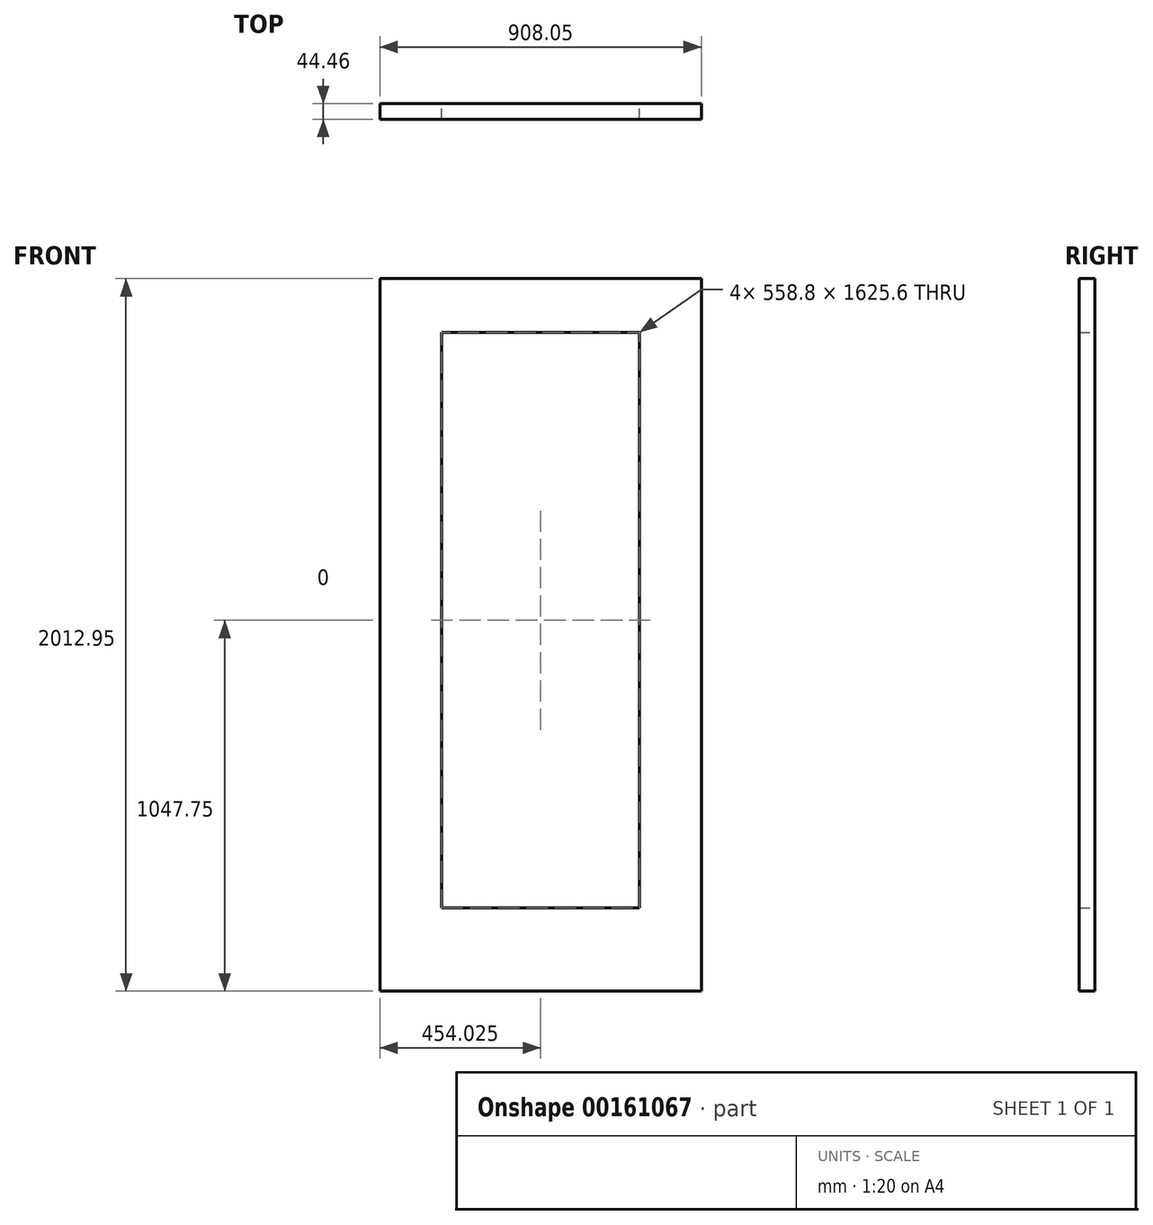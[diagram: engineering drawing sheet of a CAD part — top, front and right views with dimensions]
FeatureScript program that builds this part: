
annotation { "Feature Type Name" : "Feature", "Feature Type Description" : "" }
export const myFeature = defineFeature(function(context is Context, id is Id, definition is map)
    precondition{}
    {
        {
            var Q0;
            Q0=qCreatedBy(makeId("Front.planeOp"),FACE);
            var sketch = newSketch(context, id + "F0", { "sketchPlane" : qUnion([Q0])});
            skLineSegment(sketch, "E0.bottom", {"start": v(0, 0) * mm, "end": v(908.05, 0) * mm});
            skLineSegment(sketch, "E0.top", {"start": v(0, 2012.95) * mm, "end": v(908.05, 2012.95) * mm});
            skLineSegment(sketch, "E0.left", {"start": v(0, 0) * mm, "end": v(0, 2012.95) * mm});
            skLineSegment(sketch, "E0.right", {"start": v(908.05, 0) * mm, "end": v(908.05, 2012.95) * mm});
            skLineSegment(sketch, "E1.bottom", {"start": v(174.62, 1860.55) * mm, "end": v(733.42, 1860.55) * mm});
            skLineSegment(sketch, "E1.top", {"start": v(174.63, 234.95) * mm, "end": v(733.42, 234.95) * mm});
            skLineSegment(sketch, "E1.left", {"start": v(174.62, 1860.55) * mm, "end": v(174.63, 234.95) * mm});
            skLineSegment(sketch, "E1.right", {"start": v(733.42, 1860.55) * mm, "end": v(733.42, 234.95) * mm});
            skSolve(sketch);
        }
        {
            var Q0;
            Q0 = qSketchRegion(id + "F0", true);
            extrude(context, id + "F1", {"entities" : qUnion([Q0]), "depth" : 22.22 * mm, "hasSecondDirection" : true, "secondDirectionOppositeDirection" : true, "secondDirectionDepth" : 22.22 * mm});
        }
    });
